# Revit family: Serene_T&T_Door_Standard
name_source: partatom
category: Doors
revit_build: Autodesk Revit 2014 (Build: 20130308_1515(x64)
units: mm (PartAtom-declared; Revit-internal decimal feet)

## types (27) — shared parameters
DG Gasket Finish = Double Glazing Gasket Material
Description = Heavy duty tilt and hinged door
Frame Thickness = 52 mm
Limit Door Height Max = 2767 mm
Limit Door Height Min = 367 mm
Limit Door Width Max = 1267 mm
Limit Door Width Min = 367 mm
Limit Sash Height Max = 2700 mm  [stored 8.85827 ft]
Limit Sash Height Min = 300 mm
Limit Sash Width Max = 1200 mm
Limit Sash Width Min = 300 mm
Manufacturer = Crealco
Max System DG One Piece Thickness = 6 mm  [stored 0.019685 ft]
Max System DG Unit Thickness = 25 mm  [stored 0.082021 ft]
Model = Serene
Sash Edge Gap = 34 mm
Sash Frame Gasket = 3 mm  [stored 0.00984252 ft]
URL = http://www.crealco.co.za
Wall Closure = By host
zero-valued in all types: Custom Door Exterior Offset, Default Sill Height

## per-type parameters (varying)
| type | Clearvue Insulated LowE SHGC Value | Clearvue Insulated LowE U Value | Clearvue Insulated SHGC Value | Clearvue Insulated U Value | Custom Door Height | Custom Door Width | Custom Windload | DG Thickness Calc | Height | Intruderprufe Insulated LowE SHGC Value | Intruderprufe Insulated LowE U Value | Intruderprufe Insulated SHGC Value | Intruderprufe Insulated U Value | Intruderprufe LowE SHGC Value | Intruderprufe LowE U Value | Intruderprufe SHGC Value | Intruderprufe U Value | Max Pane Area | Sash Height | Sash Width | Width | Windload Design |
| Serene-T&T-Door-0721-1000Pa | 0.462 | 3.8 | 0.506 | 4.29 | 2090 mm  [stored 6.85696 ft] | 690 mm  [stored 2.26378 ft] | 1000 mm  [stored 3.28084 ft] | 4 mm  [stored 0.0131234 ft] | 2090 mm  [stored 6.85696 ft] | 0.392 | 3.07 | 0.451 | 4.17 | 0.465 | 4.64 | 0.525 | 6.24 | 0.88 m² | 2023 mm | 623 mm | 690 mm  [stored 2.26378 ft] | 1000 mm  [stored 3.28084 ft] |
| Serene-T&T-Door-0724-1000Pa | 0.467 | 3.75 | 0.512 | 4.25 | 2390 mm  [stored 7.84121 ft] | 690 mm  [stored 2.26378 ft] | 1000 mm  [stored 3.28084 ft] | 4 mm  [stored 0.0131234 ft] | 2390 mm  [stored 7.84121 ft] | 0.397 | 3.04 | 0.457 | 4.13 | 0.471 | 4.62 | 0.531 | 6.22 | 1.02 m² | 2323 mm | 623 mm | 690 mm  [stored 2.26378 ft] | 1000 mm  [stored 3.28084 ft] |
| Serene-T&T-Door-0727-1000Pa | 0.471 | 3.72 | 0.517 | 4.22 | 2690 mm  [stored 8.82546 ft] | 690 mm  [stored 2.26378 ft] | 1000 mm  [stored 3.28084 ft] | 4 mm  [stored 0.0131234 ft] | 2690 mm  [stored 8.82546 ft] | 0.401 | 3.01 | 0.461 | 4.1 | 0.475 | 4.62 | 0.536 | 6.21 | 1.16 m² | 2623 mm | 623 mm | 690 mm  [stored 2.26378 ft] | 1000 mm  [stored 3.28084 ft] |
| Serene-T&T-Door-0921-1000Pa | 0.497 | 3.49 | 0.546 | 4.03 | 2090 mm  [stored 6.85696 ft] | 890 mm  [stored 2.91995 ft] | 1000 mm  [stored 3.28084 ft] | 4 mm  [stored 0.0131234 ft] | 2090 mm  [stored 6.85696 ft] | 0.423 | 2.88 | 0.487 | 3.92 | 0.504 | 4.57 | 0.568 | 6.15 | 1.25 m² | 2023 mm | 823 mm  [stored 2.70013 ft] | 890 mm  [stored 2.91995 ft] | 1000 mm  [stored 3.28084 ft] |
| Serene-T&T-Door-0924-1000Pa | 0.503 | 3.44 | 0.522 | 3.99 | 2390 mm  [stored 7.84121 ft] | 890 mm  [stored 2.91995 ft] | 1000 mm  [stored 3.28084 ft] | 4 mm  [stored 0.0131234 ft] | 2390 mm  [stored 7.84121 ft] | 0.428 | 2.85 | 0.492 | 3.88 | 0.51 | 4.56 | 0.575 | 6.13 | 1.45 m² | 2323 mm | 823 mm  [stored 2.70013 ft] | 890 mm  [stored 2.91995 ft] | 1000 mm  [stored 3.28084 ft] |
| Serene-T&T-Door-0927-1000Pa | 0.508 | 3.4 | 0.557 | 3.96 | 2690 mm  [stored 8.82546 ft] | 890 mm  [stored 2.91995 ft] | 1000 mm  [stored 3.28084 ft] | 4 mm  [stored 0.0131234 ft] | 2690 mm  [stored 8.82546 ft] | 0.431 | 2.83 | 0.496 | 3.85 | 0.514 | 4.54 | 0.58 | 6.11 | 1.65 m² | 2623 mm | 823 mm  [stored 2.70013 ft] | 890 mm  [stored 2.91995 ft] | 1000 mm  [stored 3.28084 ft] |
| Serene-T&T-Door-1221-1000Pa | 0.529 | 3.22 | 0.581 | 3.81 | 2090 mm  [stored 6.85696 ft] | 1190 mm  [stored 3.9042 ft] | 1000 mm  [stored 3.28084 ft] | 4 mm  [stored 0.0131234 ft] | 2090 mm  [stored 6.85696 ft] | 0.45 | 2.72 | 0.517 | 3.7 | 0.536 | 4.51 | 0.605 | 6.06 | 1.81 m² | 2023 mm | 1123 mm | 1190 mm  [stored 3.9042 ft] | 1000 mm  [stored 3.28084 ft] |
| Serene-T&T-Door-1224-1000Pa | 0.535 | 3.17 | 0.588 | 3.77 | 2390 mm  [stored 7.84121 ft] | 1190 mm  [stored 3.9042 ft] | 1000 mm  [stored 3.28084 ft] | 4 mm  [stored 0.0131234 ft] | 2390 mm  [stored 7.84121 ft] | 0.455 | 2.69 | 0.523 | 3.66 | 0.543 | 4.49 | 0.612 | 6.04 | 2.1 m² | 2323 mm | 1123 mm | 1190 mm  [stored 3.9042 ft] | 1000 mm  [stored 3.28084 ft] |
| Serene-T&T-Door-1227-1000Pa | 0.539 | 3.13 | 0.593 | 3.78 | 2690 mm  [stored 8.82546 ft] | 1190 mm  [stored 3.9042 ft] | 1000 mm  [stored 3.28084 ft] | 5 mm  [stored 0.0164042 ft] | 2690 mm  [stored 8.82546 ft] | 0.459 | 2.66 | 0.528 | 3.62 | 0.548 | 4.48 | 0.618 | 6.03 | 2.39 m² | 2623 mm | 1123 mm | 1190 mm  [stored 3.9042 ft] | 1000 mm  [stored 3.28084 ft] |
| Serene-T&T-Door-0721-1500Pa | 0.462 | 3.8 | 0.506 | 4.29 | 2090 mm  [stored 6.85696 ft] | 690 mm  [stored 2.26378 ft] | 1500 mm  [stored 4.92126 ft] | 4 mm  [stored 0.0131234 ft] | 2090 mm  [stored 6.85696 ft] | 0.392 | 3.07 | 0.451 | 4.17 | 0.465 | 4.64 | 0.525 | 6.24 | 0.88 m² | 2023 mm | 623 mm | 690 mm  [stored 2.26378 ft] | 1500 mm  [stored 4.92126 ft] |
| Serene-T&T-Door-0721-2000Pa | 0.462 | 3.8 | 0.506 | 4.29 | 2090 mm  [stored 6.85696 ft] | 690 mm  [stored 2.26378 ft] | 2000 mm  [stored 6.56168 ft] | 4 mm  [stored 0.0131234 ft] | 2090 mm  [stored 6.85696 ft] | 0.392 | 3.07 | 0.451 | 4.17 | 0.465 | 4.64 | 0.525 | 6.24 | 0.88 m² | 2023 mm | 623 mm | 690 mm  [stored 2.26378 ft] | 2000 mm  [stored 6.56168 ft] |
| Serene-T&T-Door-0724-1500Pa | 0.467 | 3.75 | 0.512 | 4.25 | 2390 mm  [stored 7.84121 ft] | 690 mm  [stored 2.26378 ft] | 1500 mm  [stored 4.92126 ft] | 4 mm  [stored 0.0131234 ft] | 2390 mm  [stored 7.84121 ft] | 0.397 | 3.04 | 0.457 | 4.13 | 0.471 | 4.62 | 0.531 | 6.22 | 1.02 m² | 2323 mm | 623 mm | 690 mm  [stored 2.26378 ft] | 1500 mm  [stored 4.92126 ft] |
| Serene-T&T-Door-0724-2000Pa | 0.467 | 3.75 | 0.512 | 4.25 | 2390 mm  [stored 7.84121 ft] | 690 mm  [stored 2.26378 ft] | 2000 mm  [stored 6.56168 ft] | 4 mm  [stored 0.0131234 ft] | 2390 mm  [stored 7.84121 ft] | 0.397 | 3.04 | 0.457 | 4.13 | 0.471 | 4.62 | 0.531 | 6.22 | 1.02 m² | 2323 mm | 623 mm | 690 mm  [stored 2.26378 ft] | 2000 mm  [stored 6.56168 ft] |
| Serene-T&T-Door-0727-1500Pa | 0.471 | 3.72 | 0.517 | 4.22 | 2690 mm  [stored 8.82546 ft] | 690 mm  [stored 2.26378 ft] | 1500 mm  [stored 4.92126 ft] | 4 mm  [stored 0.0131234 ft] | 2690 mm  [stored 8.82546 ft] | 0.401 | 3.01 | 0.461 | 4.1 | 0.475 | 4.62 | 0.536 | 6.21 | 1.16 m² | 2623 mm | 623 mm | 690 mm  [stored 2.26378 ft] | 1500 mm  [stored 4.92126 ft] |
| Serene-T&T-Door-0727-2000Pa | 0.471 | 3.72 | 0.517 | 4.22 | 2690 mm  [stored 8.82546 ft] | 690 mm  [stored 2.26378 ft] | 2000 mm  [stored 6.56168 ft] | 4 mm  [stored 0.0131234 ft] | 2690 mm  [stored 8.82546 ft] | 0.401 | 3.01 | 0.461 | 4.1 | 0.475 | 4.62 | 0.536 | 6.21 | 1.16 m² | 2623 mm | 623 mm | 690 mm  [stored 2.26378 ft] | 2000 mm  [stored 6.56168 ft] |
| Serene-T&T-Door-0921-1500Pa | 0.497 | 3.49 | 0.546 | 4.03 | 2090 mm  [stored 6.85696 ft] | 890 mm  [stored 2.91995 ft] | 1500 mm  [stored 4.92126 ft] | 4 mm  [stored 0.0131234 ft] | 2090 mm  [stored 6.85696 ft] | 0.423 | 2.88 | 0.487 | 3.92 | 0.504 | 4.57 | 0.568 | 6.15 | 1.25 m² | 2023 mm | 823 mm  [stored 2.70013 ft] | 890 mm  [stored 2.91995 ft] | 1500 mm  [stored 4.92126 ft] |
| Serene-T&T-Door-0921-2000Pa | 0.497 | 3.49 | 0.546 | 4.03 | 2090 mm  [stored 6.85696 ft] | 890 mm  [stored 2.91995 ft] | 2000 mm  [stored 6.56168 ft] | 4 mm  [stored 0.0131234 ft] | 2090 mm  [stored 6.85696 ft] | 0.423 | 2.88 | 0.487 | 3.92 | 0.504 | 4.57 | 0.568 | 6.15 | 1.25 m² | 2023 mm | 823 mm  [stored 2.70013 ft] | 890 mm  [stored 2.91995 ft] | 2000 mm  [stored 6.56168 ft] |
| Serene-T&T-Door-0924-1500Pa | 0.503 | 3.44 | 0.522 | 3.99 | 2390 mm  [stored 7.84121 ft] | 890 mm  [stored 2.91995 ft] | 1500 mm  [stored 4.92126 ft] | 4 mm  [stored 0.0131234 ft] | 2390 mm  [stored 7.84121 ft] | 0.428 | 2.85 | 0.492 | 3.88 | 0.51 | 4.56 | 0.575 | 6.13 | 1.45 m² | 2323 mm | 823 mm  [stored 2.70013 ft] | 890 mm  [stored 2.91995 ft] | 1500 mm  [stored 4.92126 ft] |
| Serene-T&T-Door-0924-2000Pa | 0.503 | 3.44 | 0.522 | 3.99 | 2390 mm  [stored 7.84121 ft] | 890 mm  [stored 2.91995 ft] | 2000 mm  [stored 6.56168 ft] | 4 mm  [stored 0.0131234 ft] | 2390 mm  [stored 7.84121 ft] | 0.428 | 2.85 | 0.492 | 3.88 | 0.51 | 4.56 | 0.575 | 6.13 | 1.45 m² | 2323 mm | 823 mm  [stored 2.70013 ft] | 890 mm  [stored 2.91995 ft] | 2000 mm  [stored 6.56168 ft] |
| Serene-T&T-Door-0927-1500Pa | 0.508 | 3.4 | 0.557 | 3.96 | 2690 mm  [stored 8.82546 ft] | 890 mm  [stored 2.91995 ft] | 1500 mm  [stored 4.92126 ft] | 4 mm  [stored 0.0131234 ft] | 2690 mm  [stored 8.82546 ft] | 0.431 | 2.83 | 0.496 | 3.85 | 0.514 | 4.54 | 0.58 | 6.11 | 1.65 m² | 2623 mm | 823 mm  [stored 2.70013 ft] | 890 mm  [stored 2.91995 ft] | 1500 mm  [stored 4.92126 ft] |
| Serene-T&T-Door-0927-2000Pa | 0.508 | 3.4 | 0.557 | 3.96 | 2690 mm  [stored 8.82546 ft] | 890 mm  [stored 2.91995 ft] | 2000 mm  [stored 6.56168 ft] | 4 mm  [stored 0.0131234 ft] | 2690 mm  [stored 8.82546 ft] | 0.431 | 2.83 | 0.496 | 3.85 | 0.514 | 4.54 | 0.58 | 6.11 | 1.65 m² | 2623 mm | 823 mm  [stored 2.70013 ft] | 890 mm  [stored 2.91995 ft] | 2000 mm  [stored 6.56168 ft] |
| Serene-T&T-Door-1221-1500Pa | 0.529 | 3.22 | 0.581 | 3.81 | 2090 mm  [stored 6.85696 ft] | 1190 mm  [stored 3.9042 ft] | 1500 mm  [stored 4.92126 ft] | 4 mm  [stored 0.0131234 ft] | 2090 mm  [stored 6.85696 ft] | 0.45 | 2.72 | 0.517 | 3.7 | 0.536 | 4.51 | 0.605 | 6.06 | 1.81 m² | 2023 mm | 1123 mm | 1190 mm  [stored 3.9042 ft] | 1500 mm  [stored 4.92126 ft] |
| Serene-T&T-Door-1221-2000Pa | 0.529 | 3.22 | 0.581 | 3.81 | 2090 mm  [stored 6.85696 ft] | 1190 mm  [stored 3.9042 ft] | 2000 mm  [stored 6.56168 ft] | 4 mm  [stored 0.0131234 ft] | 2090 mm  [stored 6.85696 ft] | 0.45 | 2.72 | 0.517 | 3.7 | 0.536 | 4.51 | 0.605 | 6.06 | 1.81 m² | 2023 mm | 1123 mm | 1190 mm  [stored 3.9042 ft] | 2000 mm  [stored 6.56168 ft] |
| Serene-T&T-Door-1227-1500Pa | 0.539 | 3.13 | 0.593 | 3.78 | 2690 mm  [stored 8.82546 ft] | 1190 mm  [stored 3.9042 ft] | 1500 mm  [stored 4.92126 ft] | 5 mm  [stored 0.0164042 ft] | 2690 mm  [stored 8.82546 ft] | 0.459 | 2.66 | 0.528 | 3.62 | 0.548 | 4.48 | 0.618 | 6.03 | 2.39 m² | 2623 mm | 1123 mm | 1190 mm  [stored 3.9042 ft] | 1500 mm  [stored 4.92126 ft] |
| Serene-T&T-Door-1227-2000Pa | 0.539 | 3.13 | 0.593 | 3.78 | 2690 mm  [stored 8.82546 ft] | 1190 mm  [stored 3.9042 ft] | 2000 mm  [stored 6.56168 ft] | 5 mm  [stored 0.0164042 ft] | 2690 mm  [stored 8.82546 ft] | 0.459 | 2.66 | 0.528 | 3.62 | 0.548 | 4.48 | 0.618 | 6.03 | 2.39 m² | 2623 mm | 1123 mm | 1190 mm  [stored 3.9042 ft] | 2000 mm  [stored 6.56168 ft] |
| Serene-T&T-Door-1224-1500Pa | 0.535 | 3.17 | 0.588 | 3.77 | 2390 mm  [stored 7.84121 ft] | 1190 mm  [stored 3.9042 ft] | 1500 mm  [stored 4.92126 ft] | 4 mm  [stored 0.0131234 ft] | 2390 mm  [stored 7.84121 ft] | 0.455 | 2.69 | 0.523 | 3.66 | 0.543 | 4.49 | 0.612 | 6.04 | 2.1 m² | 2323 mm | 1123 mm | 1190 mm  [stored 3.9042 ft] | 1500 mm  [stored 4.92126 ft] |
| Serene-T&T-Door-1224-2000Pa | 0.535 | 3.17 | 0.588 | 3.77 | 2390 mm  [stored 7.84121 ft] | 1190 mm  [stored 3.9042 ft] | 2000 mm  [stored 6.56168 ft] | 4 mm  [stored 0.0131234 ft] | 2390 mm  [stored 7.84121 ft] | 0.455 | 2.69 | 0.523 | 3.66 | 0.543 | 4.49 | 0.612 | 6.04 | 2.1 m² | 2323 mm | 1123 mm | 1190 mm  [stored 3.9042 ft] | 2000 mm  [stored 6.56168 ft] |

note: [stored X ft] marks values corroborated as IEEE doubles in the binary element streams (Revit-internal decimal feet)

## geometry (parser evidence)
native form markers: Sweep x13
no freeform markers — native parametric forms only
